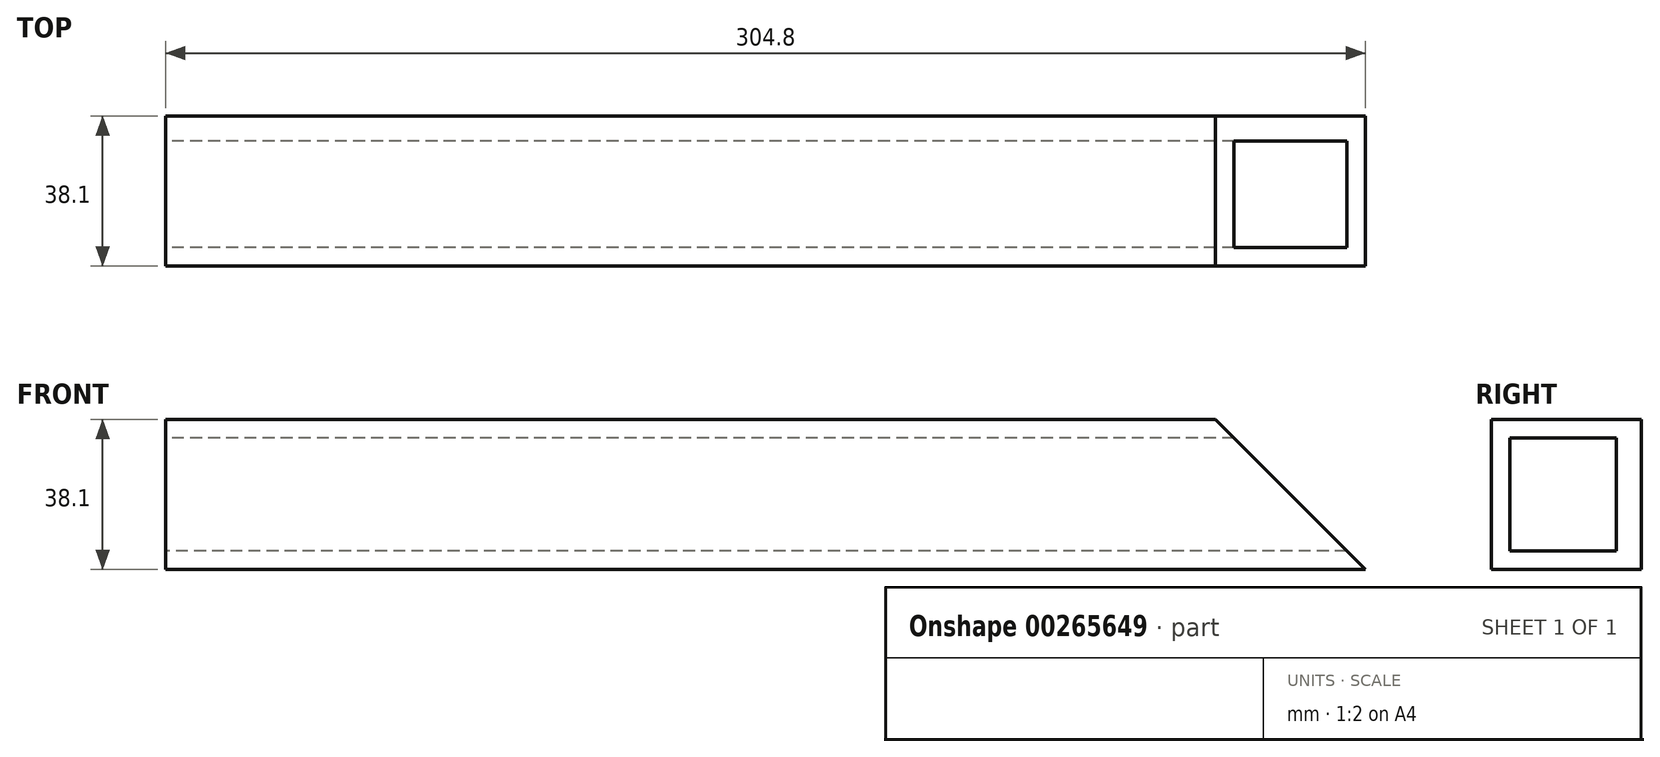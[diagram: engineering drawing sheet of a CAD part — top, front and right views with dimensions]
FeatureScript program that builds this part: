
annotation { "Feature Type Name" : "Feature", "Feature Type Description" : "" }
export const myFeature = defineFeature(function(context is Context, id is Id, definition is map)
    precondition{}
    {
        {
            var Q0;
            Q0=qCreatedBy(makeId("Right.planeOp"),FACE);
            var sketch = newSketch(context, id + "F0", { "sketchPlane" : qUnion([Q0])});
            skLineSegment(sketch, "E0.bottom", {"start": v(-19.05, 19.05) * mm, "end": v(19.05, 19.05) * mm});
            skLineSegment(sketch, "E0.top", {"start": v(-19.05, -19.05) * mm, "end": v(19.05, -19.05) * mm});
            skLineSegment(sketch, "E0.left", {"start": v(-19.05, 19.05) * mm, "end": v(-19.05, -19.05) * mm});
            skLineSegment(sketch, "E0.right", {"start": v(19.05, 19.05) * mm, "end": v(19.05, -19.05) * mm});
            skLineSegment(sketch, "E1.1", {"start": v(-19.09, 19.09) * mm, "end": v(-19.09, -19.09) * mm});
            skLineSegment(sketch, "E2.0", {"start": v(-14.31, 14.31) * mm, "end": v(12.74, 14.31) * mm});
            skLineSegment(sketch, "E2.1", {"start": v(-14.31, 14.31) * mm, "end": v(-14.31, -14.31) * mm});
            skLineSegment(sketch, "E2.2", {"start": v(-14.31, -14.31) * mm, "end": v(12.74, -14.31) * mm});
            skLineSegment(sketch, "E2.3", {"start": v(12.74, 14.31) * mm, "end": v(12.74, -14.31) * mm});
            skSolve(sketch);
        }
        {
            var Q0;
            Q0=makeQuery(id+"F0.imprint","IMPRINT",FACE,{"disambiguationData":[TD([[makeQuery(id+"F0.imprint","IMPRINT",EDGE,{"derivedFrom":sQuery(id+"F0.wireOp",EDGE,"E0.bottom")}),-1.0]])]});
            extrude(context, id + "F1", {"entities" : qUnion([Q0]), "depth" : 304.8 * mm});
        }
        {
            var Q0;
            Q0=makeQuery(id+"F1.opExtrude","SWEPT_FACE",FACE,{"disambiguationData":[OSD([sQuery(id+"F0.wireOp",EDGE,"E0.left")])]});
            var sketch = newSketch(context, id + "F2", { "sketchPlane" : qUnion([Q0])});
            skLineSegment(sketch, "E3", {"start": v(304.8, -19.05) * mm, "end": v(266.7, 19.05) * mm});
            skSolve(sketch);
        }
        {
            var Q0;
            {var subQ0=sQuery(id+"F2.wireOp",EDGE,"E3");Q0=makeQuery(id+"F2.imprint","IMPRINT",FACE,{"disambiguationData":[TD([[makeQuery(id+"F2.imprint","IMPRINT",EDGE,{"derivedFrom":subQ0}),-1.0]])]});}
            extrude(context, id + "F3", {"entities" : qUnion([Q0]), "operationType" : NewBodyOperationType.REMOVE, "endBound" : BoundingType.THROUGH_ALL, "oppositeDirection" : true, "depth" : 25.4 * mm});
        }
    });
